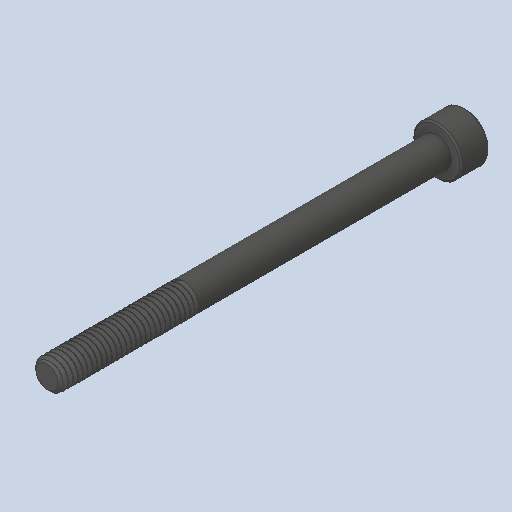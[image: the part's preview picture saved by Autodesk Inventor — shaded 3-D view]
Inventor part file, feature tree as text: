
AUTODESK INVENTOR PART (.ipt)
format: ipt  version: 2023.4 (Build 274418000, 418)  size: 662,528 bytes
history: native  units: in
note: dims shown in document units (in); Inventor stores cm internally (conversion verified against a paired STEP export)
features: chamfer x1
ambient origin geometry x8: Origin, YZ Plane, XZ Plane, XY Plane, X Axis, Y Axis, Z Axis, Center Point
bodies: Solid1 (feature_tree)
feature tree (1):
  chamfer  "Chamfer2"  [1 undecoded]
note: 1 required parameter value undecoded (feature->parameter linkage not recoverable at this tier; creation-order binding heuristic only, values carry confidence <= 0.55)
